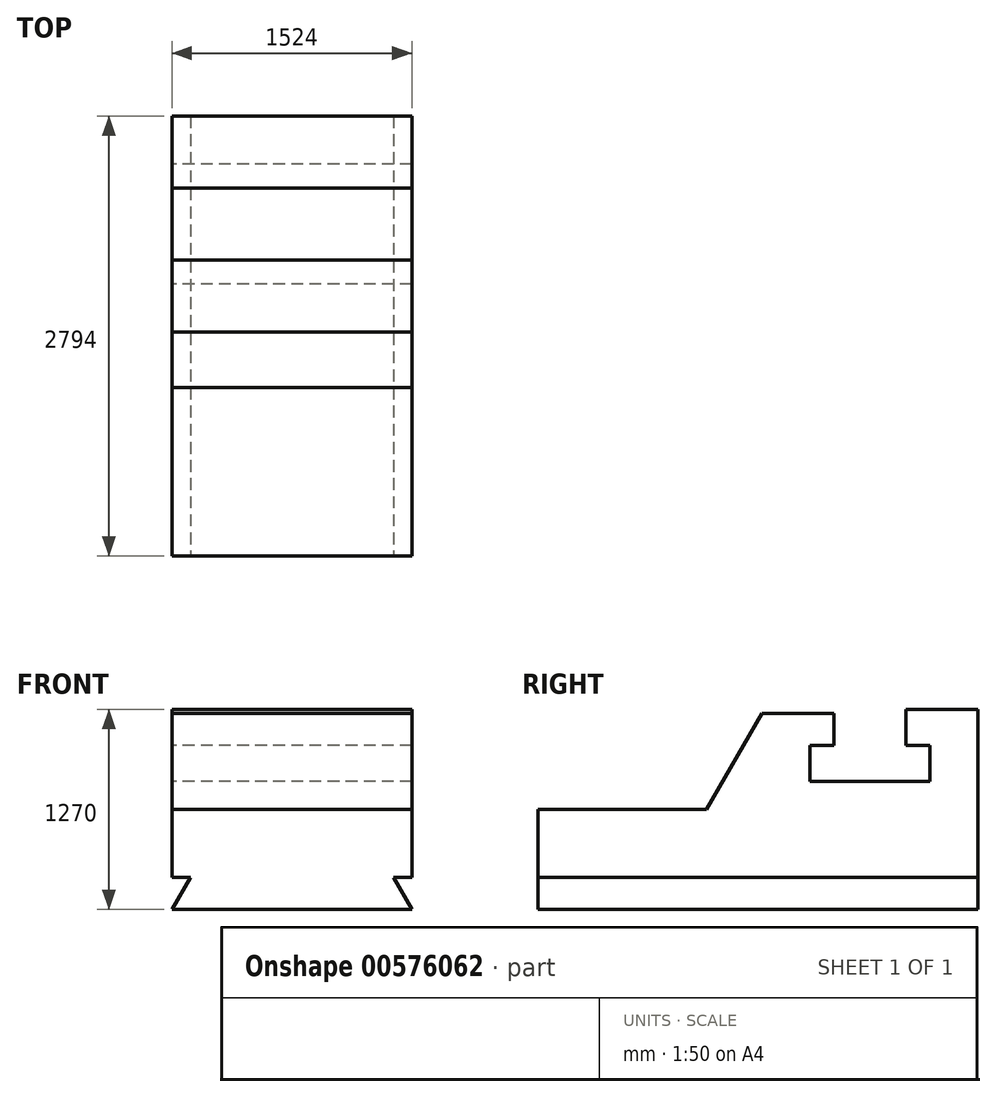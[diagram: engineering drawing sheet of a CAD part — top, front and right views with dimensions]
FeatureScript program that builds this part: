
annotation { "Feature Type Name" : "Feature", "Feature Type Description" : "" }
export const myFeature = defineFeature(function(context is Context, id is Id, definition is map)
    precondition{}
    {
        {
            var Q0;
            Q0=qCreatedBy(makeId("Right.planeOp"),FACE);
            var sketch = newSketch(context, id + "F0", { "sketchPlane" : qUnion([Q0])});
            skLineSegment(sketch, "E0", {"start": v(-317.89, -45.7) * mm, "end": v(2476.11, -45.7) * mm});
            skLineSegment(sketch, "E1", {"start": v(2476.11, -45.7) * mm, "end": v(2476.11, 1224.3) * mm});
            skLineSegment(sketch, "E2", {"start": v(2476.11, 1224.3) * mm, "end": v(2018.91, 1224.3) * mm});
            skLineSegment(sketch, "E3", {"start": v(2018.91, 1224.3) * mm, "end": v(2018.91, 995.7) * mm});
            skLineSegment(sketch, "E4", {"start": v(2018.91, 995.7) * mm, "end": v(2171.31, 995.7) * mm});
            skLineSegment(sketch, "E5", {"start": v(2171.31, 995.7) * mm, "end": v(2171.31, 767.1) * mm});
            skLineSegment(sketch, "E6", {"start": v(2171.31, 767.1) * mm, "end": v(1409.31, 767.1) * mm});
            skLineSegment(sketch, "E7", {"start": v(1409.31, 767.1) * mm, "end": v(1409.31, 995.7) * mm});
            skLineSegment(sketch, "E8", {"start": v(1409.31, 995.7) * mm, "end": v(1561.71, 995.7) * mm});
            skLineSegment(sketch, "E9", {"start": v(1561.71, 995.7) * mm, "end": v(1561.71, 1198.9) * mm});
            skLineSegment(sketch, "E10", {"start": v(1561.71, 1198.9) * mm, "end": v(1104.51, 1198.9) * mm});
            skLineSegment(sketch, "E11", {"start": v(-317.89, -45.7) * mm, "end": v(-317.89, 589.3) * mm});
            skLineSegment(sketch, "E12", {"start": v(-317.89, 589.3) * mm, "end": v(752.56, 589.3) * mm});
            skLineSegment(sketch, "E13", {"start": v(1104.51, 1198.9) * mm, "end": v(752.56, 589.3) * mm});
            skSolve(sketch);
        }
        {
            var Q0;
            Q0 = qSketchRegion(id + "F0", true);
            extrude(context, id + "F1", {"entities" : qUnion([Q0]), "depth" : 1524 * mm, "offsetDistance" : 25.4 * mm});
        }
        {
            var Q0;
            Q0=makeQuery(id+"F1.opExtrude","SWEPT_FACE",FACE,{"disambiguationData":[OSD([sQuery(id+"F0.wireOp",EDGE,"E11")])]});
            var sketch = newSketch(context, id + "F2", { "sketchPlane" : qUnion([Q0])});
            skLineSegment(sketch, "E14", {"start": v(1524, -45.7) * mm, "end": v(1524, 157.5) * mm});
            skLineSegment(sketch, "E15", {"start": v(1524, 157.5) * mm, "end": v(0, 157.5) * mm});
            skLineSegment(sketch, "E16", {"start": v(1524, -45.7) * mm, "end": v(1406.68, 157.5) * mm});
            skLineSegment(sketch, "E17", {"start": v(0, 157.5) * mm, "end": v(0, -45.7) * mm});
            skLineSegment(sketch, "E18", {"start": v(0, -45.7) * mm, "end": v(117.32, 157.5) * mm});
            skSolve(sketch);
        }
        {
            var Q0;
            {var subQ0=sQuery(id+"F2.wireOp",EDGE,"E17");Q0=makeQuery(id+"F2.imprint","IMPRINT",FACE,{"disambiguationData":[TD([[makeQuery(id+"F2.imprint","IMPRINT",EDGE,{"derivedFrom":subQ0}),-1.0]])]});}
            var Q1;
            {var subQ0=sQuery(id+"F2.wireOp",EDGE,"E14");Q1=makeQuery(id+"F2.imprint","IMPRINT",FACE,{"disambiguationData":[TD([[makeQuery(id+"F2.imprint","IMPRINT",EDGE,{"derivedFrom":subQ0}),1.0]])]});}
            extrude(context, id + "F3", {"entities" : qUnion([Q0, Q1]), "operationType" : NewBodyOperationType.REMOVE, "endBound" : BoundingType.THROUGH_ALL, "oppositeDirection" : true, "depth" : 25.4 * mm, "offsetDistance" : 25.4 * mm});
        }
    });
